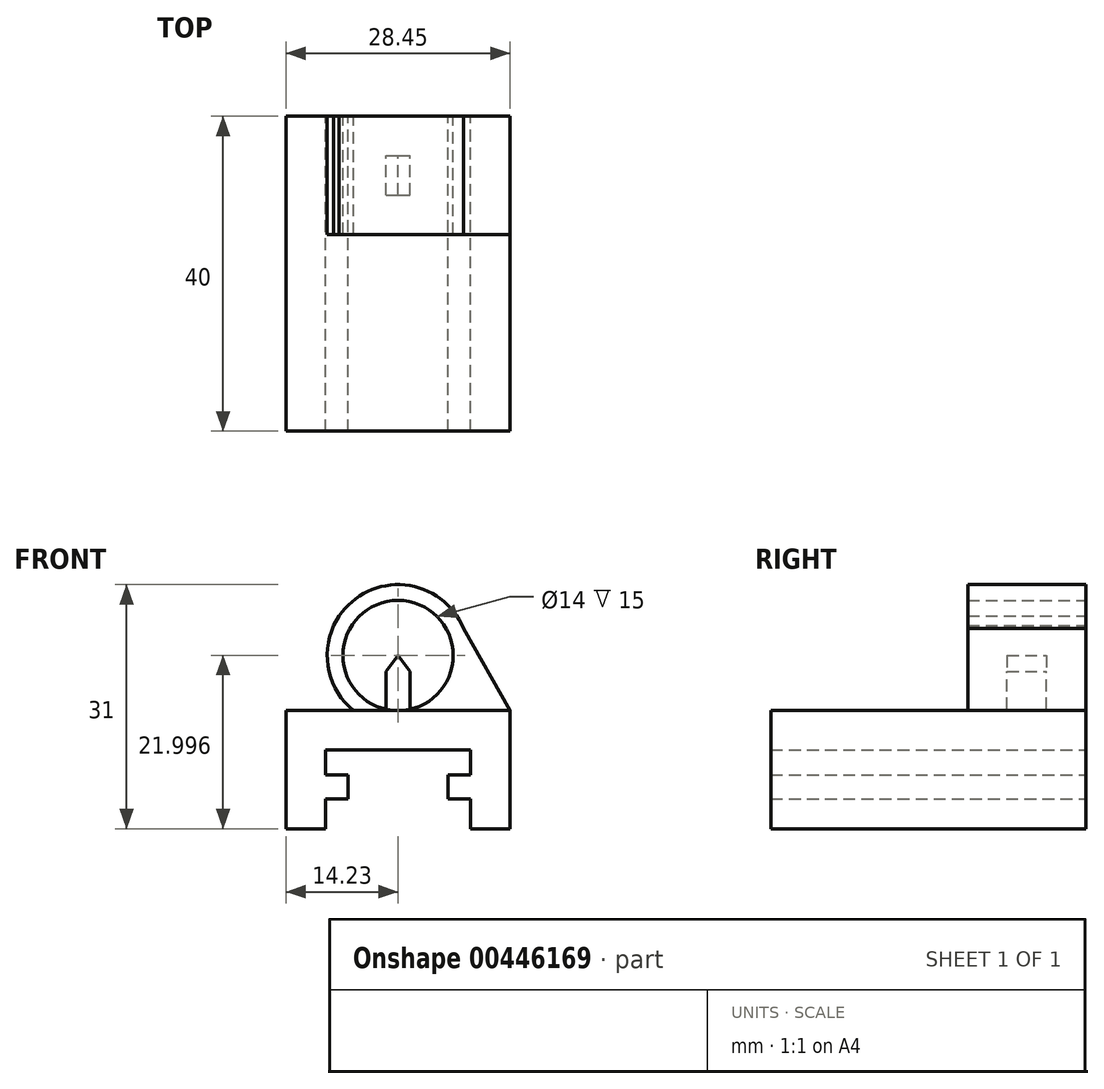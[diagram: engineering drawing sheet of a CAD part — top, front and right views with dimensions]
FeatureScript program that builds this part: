
annotation { "Feature Type Name" : "Feature", "Feature Type Description" : "" }
export const myFeature = defineFeature(function(context is Context, id is Id, definition is map)
    precondition{}
    {
        {
            var Q0;
            Q0=qCreatedBy(makeId("Front.planeOp"),FACE);
            var sketch = newSketch(context, id + "F0", { "sketchPlane" : qUnion([Q0])});
            skLineSegment(sketch, "E0", {"start": v(-6.35, 8.42) * mm, "end": v(6.35, 8.42) * mm});
            skLineSegment(sketch, "E1", {"start": v(-6.35, 8.42) * mm, "end": v(-6.35, 11.42) * mm});
            skLineSegment(sketch, "E2", {"start": v(6.35, 8.42) * mm, "end": v(6.35, 11.42) * mm});
            skLineSegment(sketch, "E3", {"start": v(-6.35, 11.42) * mm, "end": v(6.35, 11.42) * mm});
            skLineSegment(sketch, "E4", {"start": v(-6.35, 11.42) * mm, "end": v(9.23, 11.42) * mm});
            skLineSegment(sketch, "E5", {"start": v(-6.35, 11.42) * mm, "end": v(-9.23, 11.42) * mm});
            skLineSegment(sketch, "E6", {"start": v(-9.23, 11.42) * mm, "end": v(-9.23, 14.62) * mm});
            skLineSegment(sketch, "E7", {"start": v(9.23, 11.42) * mm, "end": v(9.23, 14.62) * mm});
            skLineSegment(sketch, "E8", {"start": v(-9.23, 14.62) * mm, "end": v(9.23, 14.62) * mm});
            skLineSegment(sketch, "E9", {"start": v(-9.23, 14.62) * mm, "end": v(-9.22, 4.62) * mm});
            skLineSegment(sketch, "E10", {"start": v(9.23, 14.62) * mm, "end": v(9.23, 4.62) * mm});
            skLineSegment(sketch, "E11", {"start": v(-9.23, 4.62) * mm, "end": v(9.23, 4.62) * mm});
            skLineSegment(sketch, "E12", {"start": v(-6.35, 8.42) * mm, "end": v(-6.35, 4.62) * mm});
            skLineSegment(sketch, "E13", {"start": v(6.35, 8.42) * mm, "end": v(6.35, 4.62) * mm});
            skLineSegment(sketch, "E14", {"start": v(-6.35, 8.42) * mm, "end": v(-9.23, 8.42) * mm});
            skLineSegment(sketch, "E15", {"start": v(6.35, 8.42) * mm, "end": v(9.23, 8.42) * mm});
            skLineSegment(sketch, "E16", {"start": v(-9.22, 4.62) * mm, "end": v(-14.23, 4.62) * mm});
            skLineSegment(sketch, "E17", {"start": v(9.23, 4.62) * mm, "end": v(14.23, 4.62) * mm});
            skLineSegment(sketch, "E18", {"start": v(-14.23, 4.62) * mm, "end": v(-14.23, 19.62) * mm});
            skLineSegment(sketch, "E19", {"start": v(14.23, 4.62) * mm, "end": v(14.23, 19.62) * mm});
            skLineSegment(sketch, "E20", {"start": v(-14.23, 19.62) * mm, "end": v(14.23, 19.62) * mm});
            skCircle(sketch, "E21", {"center": v(0, 26.62) * mm, "radius": 7 * mm});
            skArc(sketch, "E22", {"start": v(-5.66, 19.62) * mm, "mid": v(0, 35.62) * mm, "end": v(5.66, 19.62) * mm});
            skLineSegment(sketch, "E23", {"start": v(-7.48, 31.62) * mm, "end": v(-14.23, 19.62) * mm});
            skLineSegment(sketch, "E24", {"start": v(8.32, 30.06) * mm, "end": v(14.23, 19.62) * mm});
            skLineSegment(sketch, "E25", {"start": v(-1.5, 19.62) * mm, "end": v(-1.5, 24.62) * mm});
            skLineSegment(sketch, "E26", {"start": v(-1.5, 24.62) * mm, "end": v(0, 26.62) * mm});
            skLineSegment(sketch, "E27", {"start": v(0, 26.62) * mm, "end": v(1.5, 24.62) * mm});
            skLineSegment(sketch, "E28", {"start": v(1.5, 24.62) * mm, "end": v(1.5, 19.62) * mm});
            skSolve(sketch);
        }
        {
            var Q0;
            {var subQ6=sQuery(id+"F0.wireOp",EDGE,"E8");Q0=makeQuery(id+"F0.imprint","IMPRINT",FACE,{"disambiguationData":[TD([[makeQuery(id+"F0.imprint","IMPRINT",EDGE,{"derivedFrom":subQ6}),1.0]])]});}
            var Q1;
            Q1=makeQuery(id+"F0.imprint","IMPRINT",FACE,{"disambiguationData":[TD([[makeQuery(id+"F0.imprint","IMPRINT",EDGE,{"derivedFrom":sQuery(id+"F0.wireOp",EDGE,"E1")}),1.0]])]});
            var Q2;
            {var subQ0=sQuery(id+"F0.wireOp",EDGE,"E2");Q2=makeQuery(id+"F0.imprint","IMPRINT",FACE,{"disambiguationData":[TD([[makeQuery(id+"F0.imprint","IMPRINT",EDGE,{"derivedFrom":subQ0}),-1.0]])]});}
            extrude(context, id + "F1", {"entities" : qUnion([Q0, Q1, Q2]), "depth" : 40 * mm});
        }
        {
            var Q0;
            {var subQ1=sQuery(id+"F0.wireOp",EDGE,"E20");var subQ3=sQuery(id+"F0.wireOp",EDGE,"E22");var subQ4=makeQuery(id+"F0.imprint","INTERSECT",VERTEX,{"disambiguationData":[OD(0.0)],"derivedFrom":[subQ1,subQ3]});Q0=makeQuery(id+"F0.imprint","IMPRINT",FACE,{"disambiguationData":[TD([[makeQuery(id+"F0.imprint","IMPRINT",EDGE,{"disambiguationData":[TD([[subQ4,-1.0]])],"derivedFrom":subQ3}),1.0]])]});}
            var Q1;
            {var subQ5=sQuery(id+"F0.wireOp",EDGE,"E22");var subQ6=sQuery(id+"F0.wireOp",EDGE,"E20");var subQ7=makeQuery(id+"F0.imprint","INTERSECT",VERTEX,{"disambiguationData":[OD(0.0)],"derivedFrom":[subQ6,subQ5]});Q1=makeQuery(id+"F0.imprint","IMPRINT",FACE,{"disambiguationData":[TD([[makeQuery(id+"F0.imprint","IMPRINT",EDGE,{"disambiguationData":[TD([[subQ7,-1.0]])],"derivedFrom":subQ6}),1.0]])]});}
            var Q2;
            {var subQ0=sQuery(id+"F0.wireOp",EDGE,"E24");Q2=makeQuery(id+"F0.imprint","IMPRINT",FACE,{"disambiguationData":[TD([[makeQuery(id+"F0.imprint","IMPRINT",EDGE,{"derivedFrom":subQ0}),-1.0]])]});}
            extrude(context, id + "F2", {"entities" : qUnion([Q0, Q1, Q2]), "operationType" : NewBodyOperationType.ADD, "depth" : 15 * mm});
        }
        {
            var Q0;
            {var subQ0=sQuery(id+"F0.wireOp",EDGE,"E26");Q0=makeQuery(id+"F0.imprint","IMPRINT",FACE,{"disambiguationData":[TD([[makeQuery(id+"F0.imprint","IMPRINT",EDGE,{"derivedFrom":subQ0}),-1.0]])]});}
            var Q1;
            {var subQ0=sQuery(id+"F0.wireOp",EDGE,"E25");var subQ1=sQuery(id+"F0.wireOp",EDGE,"E20");var subQ2=makeQuery(id+"F0.imprint","INTERSECT",VERTEX,{"derivedFrom":[subQ1,subQ0]});Q1=makeQuery(id+"F0.imprint","IMPRINT",FACE,{"disambiguationData":[TD([[makeQuery(id+"F0.imprint","IMPRINT",EDGE,{"disambiguationData":[TD([[subQ2,-1.0]])],"derivedFrom":subQ1}),1.0]])]});}
            var Q2;
            {var subQ0=sQuery(id+"F0.wireOp",EDGE,"E28");var subQ1=sQuery(id+"F0.wireOp",EDGE,"E20");var subQ2=makeQuery(id+"F0.imprint","INTERSECT",VERTEX,{"derivedFrom":[subQ1,subQ0]});Q2=makeQuery(id+"F0.imprint","IMPRINT",FACE,{"disambiguationData":[TD([[makeQuery(id+"F0.imprint","IMPRINT",EDGE,{"disambiguationData":[TD([[subQ2,1.0]])],"derivedFrom":subQ1}),1.0]])]});}
            extrude(context, id + "F3", {"entities" : qUnion([Q0, Q1, Q2]), "operationType" : NewBodyOperationType.ADD, "depth" : 10 * mm});
        }
        {
            var Q0;
            {var subQ0=sQuery(id+"F0.wireOp",EDGE,"E28");var subQ1=sQuery(id+"F0.wireOp",EDGE,"E20");var subQ2=makeQuery(id+"F0.imprint","INTERSECT",VERTEX,{"derivedFrom":[subQ1,subQ0]});Q0=makeQuery(id+"F0.imprint","IMPRINT",FACE,{"disambiguationData":[TD([[makeQuery(id+"F0.imprint","IMPRINT",EDGE,{"disambiguationData":[TD([[subQ2,1.0]])],"derivedFrom":subQ1}),1.0]])]});}
            var Q1;
            {var subQ0=sQuery(id+"F0.wireOp",EDGE,"E25");var subQ1=sQuery(id+"F0.wireOp",EDGE,"E20");var subQ2=makeQuery(id+"F0.imprint","INTERSECT",VERTEX,{"derivedFrom":[subQ1,subQ0]});Q1=makeQuery(id+"F0.imprint","IMPRINT",FACE,{"disambiguationData":[TD([[makeQuery(id+"F0.imprint","IMPRINT",EDGE,{"disambiguationData":[TD([[subQ2,-1.0]])],"derivedFrom":subQ1}),1.0]])]});}
            extrude(context, id + "F4", {"entities" : qUnion([Q0, Q1]), "operationType" : NewBodyOperationType.ADD, "depth" : 15 * mm});
        }
        {
            var Q0;
            {var subQ0=sQuery(id+"F0.wireOp",EDGE,"E26");Q0=makeQuery(id+"F0.imprint","IMPRINT",FACE,{"disambiguationData":[TD([[makeQuery(id+"F0.imprint","IMPRINT",EDGE,{"derivedFrom":subQ0}),-1.0]])]});}
            extrude(context, id + "F5", {"entities" : qUnion([Q0]), "operationType" : NewBodyOperationType.REMOVE, "depth" : 5 * mm});
        }
    });
